# Revit family: Shinhoo_PROMO
name_source: partatom
category: Оборудование
units: mm (PartAtom-declared; Revit-internal decimal feet)

## family parameters
Всегда вертикально = Нет
Классификация = Нет
На основе рабочей плоскости = Нет
Общий = Нет
При загрузке вырезать с полостями = Нет
Размер круглого соединителя = Использовать диаметр
Тип детали = Вставляется
Точка расчета площади = Нет

## types (2) — shared parameters
ADSK_URL страницы изделия = https://shinhoopump.ru
ADSK_Версия Revit = 2019
ADSK_Версия семейства = 1.0
ADSK_Единица измерения = шт
ADSK_Завод-изготовитель = Shinhoo
ADSK_Количество = 1
ADSK_Коэффициент мощности = 1
ADSK_Материал = Чугун с катафорезным покрытием
ADSK_Напряжение = 230 В
ADSK_Обозначение = ГОСТ 31839-2012, ГОСТ 12.2.007.0-75, ГОСТ 12.2.003-91, ГОСТ Р МЭК 60204-1-2007,  ГОСТ 30804
ADSK_Ток = 1 А
DN = 20 мм
URL = https://shinhoopump.ru
rn = 10 мм
rn_1 = 11 мм
Изготовитель = Shinhoo
Класс защиты (IP) = IP43
Разработчик = ООО ПРОРУБИМ
Разработчик (телефон) = +7(495)649-85-43
Скорость вращения = 2850
Степень защиты от удара (IK) = IK04
Тип Насоса = Повысительный насос с «мокрым» ротором
Тип основания = встроенный

## per-type parameters (varying)
| type | ADSK_Код изделия | ADSK_Масса | ADSK_Масса_Текст | ADSK_Наименование | ADSK_Наименование краткое | ADSK_Номинальная мощность | ADSK_Полная мощность | ADSK_Расход жидкости | B | B1 | B2 | H | H1 | H2 | L | b1_10 | b1_5 | l_8 | Группа модели |
| PROMO 15-9A 160 1x230В - 71411001 | 71411001 | 2.7 | 2.7 | Повысительный насос с «мокрым» ротором PROMO 15-9A 160 1x230В | PROMO 15-9A 160 1x230В | 120 Вт | 120 В·А | 0.000486 м³/с | 104 мм | 50 мм | 54 мм | 126 мм | 23 мм | 103 мм | 160 мм | 40 мм | 45 мм | 20 мм | PROMO 15-9A |
| PROMO 15-12A 200 1x230В - 71411002 | 71411002 | 2.5 | 2.5 | Повысительный насос с «мокрым» ротором PROMO 15-12A 200 1x230В | PROMO 15-12A 200 1x230В | 270 Вт | 270 В·А | 0.000778 м³/с | 132 мм | 63 мм | 69 мм | 150 мм | 18 мм | 132 мм | 200 мм | 53 мм | 58 мм | 25 мм | PROMO 15-12A |

## geometry (parser evidence)
native form markers: Sweep x2
no freeform markers — native parametric forms only
